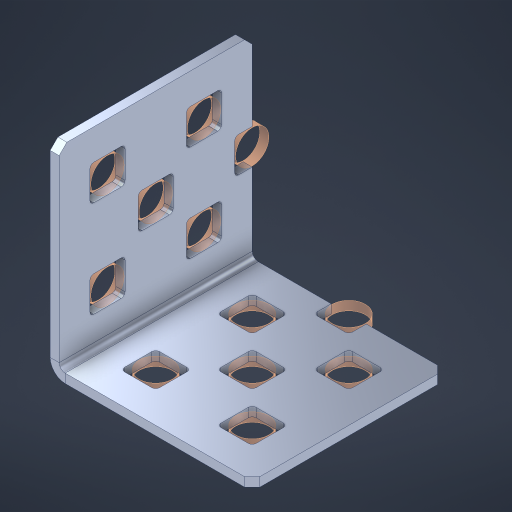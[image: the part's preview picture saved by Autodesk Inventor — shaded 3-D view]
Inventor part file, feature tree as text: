
AUTODESK INVENTOR PART (.ipt)
format: ipt  version: 2023 (Build 270158000, 158)  size: 479,744 bytes
history: native  units: in
note: dims shown in document units (in); Inventor stores cm internally (conversion verified against a paired STEP export)
features: other x18, extrude x10, sheet_metal_op x8, sketch x7, pattern_linear x2, mirror x1, chamfer x1
ambient origin geometry x8: Origin, YZ Plane, XZ Plane, XY Plane, X Axis, Y Axis, Z Axis, Center Point
bodies: Solid1 (feature_tree), Body (feature_tree)
feature tree (47):
  sheet_metal_op  "Flanges"
  sheet_metal_op  "Body Pattern"
  pattern_linear  "Center Pattern"  Spacing1=1.0in  [1 undecoded]
  other  "Arc Length"
  pattern_linear  "Notch Pattern"  Spacing1=0.1875in  [1 undecoded]
  other  "Diagonal Plane"
  mirror  "Everything Mirrored"
  chamfer  "End Chamfer"
  sketch  "Sketch1"  dims[d0=1.0in]
  other  "Plate1"
  sketch  "Sketch2"  dims[d1=1.0in]
  other  "Plate2"
  sheet_metal_op  "Bend1"
  sheet_metal_op  "Corner1"
  sketch  "Sketch8"  dims[d2=0.0469in]
  sketch  "Sketch9"  dims[d3=0.0469in]
  other  "Srf91"
  sheet_metal_op  "Body Pattern Sketch"
  other  "Srf92"
  sketch  "Sketch13"  dims[d4=0.0234in]
  sketch  "Sketch15"  dims[d5=0.0938in]
  sketch  "Sketch16"  dims[d6=0.0469in d7=1.0in d8=90.0deg d9=0.0312in d10=0.1875in d11=0.0469in d12=0.0469in d49=0.182in d50=0.02in d52=0.25in d53=0.0469in d54=0.0in d55=0.172in d56=1.0in d57=0.0in d60=0.7874in d62=0.5in d63=0.7874in d65=0.5in d85=0.1473in d86=0.1659in d89=0.0469in d90=0.0in d91=0.04in d92=0.0491in d95=2.5in d96=0.04in d97=0.25in d98=45.0deg d99=0.25in d106=0.182in d107=0.02in d108=0.5in d110=0.0469in d111=0.0in d112=0.172in d113=0.5in d114=0.0in d117=0.5in d123=0.25in d125=0.25in d126=0.0491in d127=0.1227in d128=0.08in d129=0.04in d130=2.5in]
  other  "Srf786"
  other  "Srf856"
  other  "Srf857"
  other  "Srf889"
  other  "Srf1275"
  other  "Srf1276"
  other  "Srf1278"
  other  "Srf1279"
  other  "Srf1277"
  other  "Srf1285"
  sheet_metal_op  "Body Stamp"
  sheet_metal_op  "Body Circle"
  other  "Center Stamp"
  other  "Center Circle"
  sheet_metal_op  "Notch"
  extrude  "ExtrusionSrf92"  Depth=0.0469in
  extrude  "ExtrusionSrf856"  Depth=0.0469in
  extrude  "ExtrusionSrf857"  Depth=0.182in
  extrude  "ExtrusionSrf889"  Depth=0.02in
  extrude  "ExtrusionSrf1275"  Depth=0.25in
  extrude  "ExtrusionSrf1276"  Depth=0.0469in
  extrude  "ExtrusionSrf1277"  TaperAngle=0.0deg  [1 undecoded]
  extrude  "ExtrusionSrf1278"  Depth=0.25in
  extrude  "ExtrusionSrf1345"  Depth=1.0in TaperAngle=0.0deg
  extrude  "ExtrusionSrf1346"  Depth=0.25in
note: 3 required parameter values undecoded (feature->parameter linkage not recoverable at this tier; creation-order binding heuristic only, values carry confidence <= 0.55)
